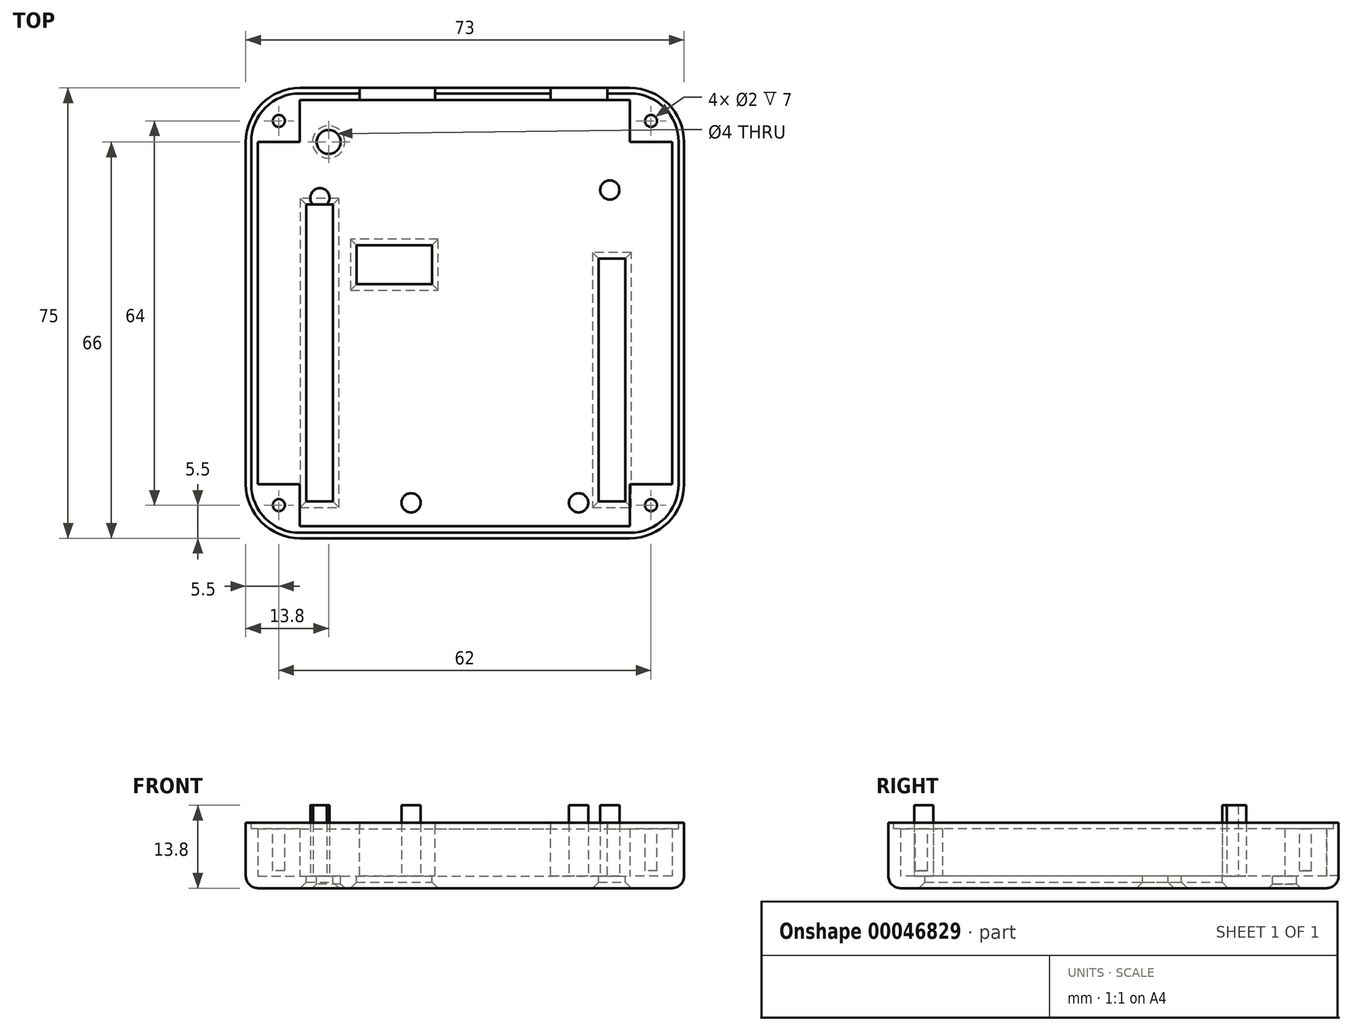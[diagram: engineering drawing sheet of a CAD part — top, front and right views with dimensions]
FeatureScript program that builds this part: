
annotation { "Feature Type Name" : "Feature", "Feature Type Description" : "" }
export const myFeature = defineFeature(function(context is Context, id is Id, definition is map)
    precondition{}
    {
        {
            var Q0;
            Q0=qCreatedBy(makeId("Top.planeOp"),FACE);
            var sketch = newSketch(context, id + "F0", { "sketchPlane" : qUnion([Q0])});
            skLineSegment(sketch, "E0.bottom", {"start": v(-27.5, 38.5) * mm, "end": v(27.5, 38.5) * mm});
            skLineSegment(sketch, "E0.top", {"start": v(-27.5, -36.5) * mm, "end": v(27.5, -36.5) * mm});
            skLineSegment(sketch, "E0.left", {"start": v(-36.5, 29.5) * mm, "end": v(-36.5, -27.5) * mm});
            skLineSegment(sketch, "E0.right", {"start": v(36.5, 29.5) * mm, "end": v(36.5, -27.5) * mm});
            skPoint(sketch, "E1.visualSharp", {"position": v(-36.5, 38.5) * mm});
            skArc(sketch, "E1.filletArc", {"start": v(-27.5, 38.5) * mm, "mid": v(-33.86, 35.86) * mm, "end": v(-36.5, 29.5) * mm});
            skPoint(sketch, "E2.visualSharp", {"position": v(36.5, 38.5) * mm});
            skArc(sketch, "E2.filletArc", {"start": v(36.5, 29.5) * mm, "mid": v(33.86, 35.86) * mm, "end": v(27.5, 38.5) * mm});
            skPoint(sketch, "E3.visualSharp", {"position": v(36.5, -36.5) * mm});
            skArc(sketch, "E3.filletArc", {"start": v(27.5, -36.5) * mm, "mid": v(33.86, -33.86) * mm, "end": v(36.5, -27.5) * mm});
            skPoint(sketch, "E4.visualSharp", {"position": v(-36.5, -36.5) * mm});
            skArc(sketch, "E4.filletArc", {"start": v(-36.5, -27.5) * mm, "mid": v(-33.86, -33.86) * mm, "end": v(-27.5, -36.5) * mm});
            skSolve(sketch);
        }
        {
            var Q0;
            Q0 = qSketchRegion(id + "F0", true);
            extrude(context, id + "F1", {"entities" : qUnion([Q0]), "depth" : 2 * mm});
        }
        {
            var Q0;
            Q0=makeQuery(id+"F1.opExtrude","CAP_FACE",FACE,{"disambiguationData":[OSD([sQuery(id+"F0.wireOp",EDGE,"E0.bottom"),sQuery(id+"F0.wireOp",EDGE,"E0.top"),sQuery(id+"F0.wireOp",EDGE,"E0.left"),sQuery(id+"F0.wireOp",EDGE,"E0.right"),sQuery(id+"F0.wireOp",EDGE,"E1.filletArc"),sQuery(id+"F0.wireOp",EDGE,"E2.filletArc"),sQuery(id+"F0.wireOp",EDGE,"E3.filletArc"),sQuery(id+"F0.wireOp",EDGE,"E4.filletArc")])],"isStart":false});
            var sketch = newSketch(context, id + "F2", { "sketchPlane" : qUnion([Q0])});
            skCircle(sketch, "E5.MirrorC", {"center": v(-24.16, 20.2) * mm, "radius": 1.6 * mm});
            skCircle(sketch, "E6.MirrorC", {"center": v(24.14, 21.5) * mm, "radius": 1.6 * mm});
            skCircle(sketch, "E7.MirrorC", {"center": v(18.94, -30.6) * mm, "radius": 1.6 * mm});
            skCircle(sketch, "E8.MirrorC", {"center": v(-8.96, -30.6) * mm, "radius": 1.6 * mm});
            skSolve(sketch);
        }
        {
            var Q0;
            Q0 = qSketchRegion(id + "F2", true);
            extrude(context, id + "F3", {"entities" : qUnion([Q0]), "operationType" : NewBodyOperationType.ADD, "depth" : 11.8 * mm});
        }
        {
            var Q0;
            Q0=makeQuery(id+"F1.opExtrude","CAP_FACE",FACE,{"disambiguationData":[OSD([sQuery(id+"F0.wireOp",EDGE,"E0.bottom"),sQuery(id+"F0.wireOp",EDGE,"E0.top"),sQuery(id+"F0.wireOp",EDGE,"E0.left"),sQuery(id+"F0.wireOp",EDGE,"E0.right"),sQuery(id+"F0.wireOp",EDGE,"E1.filletArc"),sQuery(id+"F0.wireOp",EDGE,"E2.filletArc"),sQuery(id+"F0.wireOp",EDGE,"E3.filletArc"),sQuery(id+"F0.wireOp",EDGE,"E4.filletArc")])],"isStart":false});
            var sketch = newSketch(context, id + "F4", { "sketchPlane" : qUnion([Q0])});
            skLineSegment(sketch, "E9", {"start": v(-27.5, 36.5) * mm, "end": v(27.5, 36.5) * mm});
            skLineSegment(sketch, "E10", {"start": v(-34.5, 29.5) * mm, "end": v(-34.5, -27.5) * mm});
            skLineSegment(sketch, "E11", {"start": v(-27.5, -34.5) * mm, "end": v(27.5, -34.5) * mm});
            skLineSegment(sketch, "E12", {"start": v(34.5, -27.5) * mm, "end": v(34.5, 29.5) * mm});
            skArc(sketch, "E13", {"start": v(-27.5, 36.5) * mm, "mid": v(-32.45, 34.45) * mm, "end": v(-34.5, 29.5) * mm});
            skArc(sketch, "E14", {"start": v(27.5, -34.5) * mm, "mid": v(32.45, -32.45) * mm, "end": v(34.5, -27.5) * mm});
            skArc(sketch, "E15", {"start": v(-34.5, -27.5) * mm, "mid": v(-32.45, -32.45) * mm, "end": v(-27.5, -34.5) * mm});
            skArc(sketch, "E16", {"start": v(34.5, 29.5) * mm, "mid": v(32.45, 34.45) * mm, "end": v(27.5, 36.5) * mm});
            skLineSegment(sketch, "E17.0", {"start": v(-27.5, 38.5) * mm, "end": v(27.5, 38.5) * mm});
            skArc(sketch, "E17.1", {"start": v(36.5, 29.5) * mm, "mid": v(33.86, 35.86) * mm, "end": v(27.5, 38.5) * mm});
            skLineSegment(sketch, "E17.2", {"start": v(36.5, 29.5) * mm, "end": v(36.5, -27.5) * mm});
            skArc(sketch, "E17.3", {"start": v(27.5, -36.5) * mm, "mid": v(33.86, -33.86) * mm, "end": v(36.5, -27.5) * mm});
            skLineSegment(sketch, "E17.4", {"start": v(-27.5, -36.5) * mm, "end": v(27.5, -36.5) * mm});
            skArc(sketch, "E17.5", {"start": v(-36.5, -27.5) * mm, "mid": v(-33.86, -33.86) * mm, "end": v(-27.5, -36.5) * mm});
            skLineSegment(sketch, "E17.6", {"start": v(-36.5, 29.5) * mm, "end": v(-36.5, -27.5) * mm});
            skArc(sketch, "E17.7", {"start": v(-27.5, 38.5) * mm, "mid": v(-33.86, 35.86) * mm, "end": v(-36.5, 29.5) * mm});
            skSolve(sketch);
        }
        {
            var Q0;
            Q0 = qSketchRegion(id + "F4", true);
            extrude(context, id + "F5", {"entities" : qUnion([Q0]), "operationType" : NewBodyOperationType.ADD, "depth" : 8.9 * mm});
        }
        {
            var Q0;
            Q0=makeQuery(id+"F5.opExtrude","CAP_FACE",FACE,{"disambiguationData":[OSD([sQuery(id+"F4.wireOp",EDGE,"E9"),sQuery(id+"F4.wireOp",EDGE,"E10"),sQuery(id+"F4.wireOp",EDGE,"E11"),sQuery(id+"F4.wireOp",EDGE,"E12"),sQuery(id+"F4.wireOp",EDGE,"E13"),sQuery(id+"F4.wireOp",EDGE,"E14"),sQuery(id+"F4.wireOp",EDGE,"E15"),sQuery(id+"F4.wireOp",EDGE,"E16"),sQuery(id+"F4.wireOp",EDGE,"E17.0"),sQuery(id+"F4.wireOp",EDGE,"E17.1"),sQuery(id+"F4.wireOp",EDGE,"E17.2"),sQuery(id+"F4.wireOp",EDGE,"E17.3"),sQuery(id+"F4.wireOp",EDGE,"E17.4"),sQuery(id+"F4.wireOp",EDGE,"E17.5"),sQuery(id+"F4.wireOp",EDGE,"E17.6"),sQuery(id+"F4.wireOp",EDGE,"E17.7")])],"isStart":false});
            var sketch = newSketch(context, id + "F6", { "sketchPlane" : qUnion([Q0])});
            skLineSegment(sketch, "E18", {"start": v(-27.5, 37.6) * mm, "end": v(27.5, 37.6) * mm});
            skLineSegment(sketch, "E19", {"start": v(-27.5, -35.6) * mm, "end": v(27.5, -35.6) * mm});
            skLineSegment(sketch, "E20", {"start": v(-35.6, 29.5) * mm, "end": v(-35.6, -27.5) * mm});
            skLineSegment(sketch, "E21", {"start": v(35.6, 29.5) * mm, "end": v(35.6, -27.5) * mm});
            skLineSegment(sketch, "E22.0", {"start": v(-27.5, 36.5) * mm, "end": v(27.5, 36.5) * mm});
            skArc(sketch, "E22.1", {"start": v(34.5, 29.5) * mm, "mid": v(32.45, 34.45) * mm, "end": v(27.5, 36.5) * mm});
            skLineSegment(sketch, "E22.2", {"start": v(34.5, -27.5) * mm, "end": v(34.5, 29.5) * mm});
            skArc(sketch, "E22.3", {"start": v(27.5, -34.5) * mm, "mid": v(32.45, -32.45) * mm, "end": v(34.5, -27.5) * mm});
            skLineSegment(sketch, "E22.4", {"start": v(-27.5, -34.5) * mm, "end": v(27.5, -34.5) * mm});
            skArc(sketch, "E22.5", {"start": v(-34.5, -27.5) * mm, "mid": v(-32.45, -32.45) * mm, "end": v(-27.5, -34.5) * mm});
            skLineSegment(sketch, "E22.6", {"start": v(-34.5, 29.5) * mm, "end": v(-34.5, -27.5) * mm});
            skArc(sketch, "E22.7", {"start": v(-27.5, 36.5) * mm, "mid": v(-32.45, 34.45) * mm, "end": v(-34.5, 29.5) * mm});
            skArc(sketch, "E23", {"start": v(-27.5, 37.6) * mm, "mid": v(-33.23, 35.23) * mm, "end": v(-35.6, 29.5) * mm});
            skArc(sketch, "E24", {"start": v(35.6, 29.5) * mm, "mid": v(33.23, 35.23) * mm, "end": v(27.5, 37.6) * mm});
            skArc(sketch, "E25", {"start": v(27.5, -35.6) * mm, "mid": v(33.23, -33.23) * mm, "end": v(35.6, -27.5) * mm});
            skArc(sketch, "E26", {"start": v(-35.6, -27.5) * mm, "mid": v(-33.23, -33.23) * mm, "end": v(-27.5, -35.6) * mm});
            skSolve(sketch);
        }
        {
            var Q0;
            Q0 = qSketchRegion(id + "F6", true);
            extrude(context, id + "F7", {"entities" : qUnion([Q0]), "operationType" : NewBodyOperationType.REMOVE, "oppositeDirection" : true, "depth" : 1 * mm});
        }
        {
            var Q0;
            Q0=makeQuery(id+"F5.opExtrude","CAP_FACE",FACE,{"disambiguationData":[OSD([sQuery(id+"F4.wireOp",EDGE,"E9"),sQuery(id+"F4.wireOp",EDGE,"E10"),sQuery(id+"F4.wireOp",EDGE,"E11"),sQuery(id+"F4.wireOp",EDGE,"E12"),sQuery(id+"F4.wireOp",EDGE,"E13"),sQuery(id+"F4.wireOp",EDGE,"E14"),sQuery(id+"F4.wireOp",EDGE,"E15"),sQuery(id+"F4.wireOp",EDGE,"E16"),sQuery(id+"F4.wireOp",EDGE,"E17.0"),sQuery(id+"F4.wireOp",EDGE,"E17.1"),sQuery(id+"F4.wireOp",EDGE,"E17.2"),sQuery(id+"F4.wireOp",EDGE,"E17.3"),sQuery(id+"F4.wireOp",EDGE,"E17.4"),sQuery(id+"F4.wireOp",EDGE,"E17.5"),sQuery(id+"F4.wireOp",EDGE,"E17.6"),sQuery(id+"F4.wireOp",EDGE,"E17.7")])],"isStart":false});
            var sketch = newSketch(context, id + "F8", { "sketchPlane" : qUnion([Q0])});
            skLineSegment(sketch, "E27.bottom", {"start": v(-17.56, 38.5) * mm, "end": v(-4.96, 38.5) * mm});
            skLineSegment(sketch, "E27.top", {"start": v(-17.56, 36.5) * mm, "end": v(-4.96, 36.5) * mm});
            skLineSegment(sketch, "E27.left", {"start": v(-17.56, 38.5) * mm, "end": v(-17.56, 36.5) * mm});
            skLineSegment(sketch, "E27.right", {"start": v(-4.96, 38.5) * mm, "end": v(-4.96, 36.5) * mm});
            skLineSegment(sketch, "E28.bottom", {"start": v(14.24, 38.5) * mm, "end": v(23.74, 38.5) * mm});
            skLineSegment(sketch, "E28.top", {"start": v(14.24, 36.5) * mm, "end": v(23.74, 36.5) * mm});
            skLineSegment(sketch, "E28.left", {"start": v(14.24, 38.5) * mm, "end": v(14.24, 36.5) * mm});
            skLineSegment(sketch, "E28.right", {"start": v(23.74, 38.5) * mm, "end": v(23.74, 36.5) * mm});
            skSolve(sketch);
        }
        {
            var Q0;
            Q0 = qSketchRegion(id + "F8", true);
            extrude(context, id + "F9", {"entities" : qUnion([Q0]), "operationType" : NewBodyOperationType.REMOVE, "oppositeDirection" : true, "depth" : 8.8 * mm});
        }
        {
            var Q0;
            Q0=makeQuery(id+"F1.opExtrude","CAP_FACE",FACE,{"disambiguationData":[OSD([sQuery(id+"F0.wireOp",EDGE,"E0.bottom"),sQuery(id+"F0.wireOp",EDGE,"E0.top"),sQuery(id+"F0.wireOp",EDGE,"E0.left"),sQuery(id+"F0.wireOp",EDGE,"E0.right"),sQuery(id+"F0.wireOp",EDGE,"E1.filletArc"),sQuery(id+"F0.wireOp",EDGE,"E2.filletArc"),sQuery(id+"F0.wireOp",EDGE,"E3.filletArc"),sQuery(id+"F0.wireOp",EDGE,"E4.filletArc")])],"isStart":false});
            var sketch = newSketch(context, id + "F10", { "sketchPlane" : qUnion([Q0])});
            skLineSegment(sketch, "E29.bottom", {"start": v(-26.46, 19.1) * mm, "end": v(-21.96, 19.1) * mm});
            skLineSegment(sketch, "E29.top", {"start": v(-26.46, -30.4) * mm, "end": v(-21.96, -30.4) * mm});
            skLineSegment(sketch, "E29.left", {"start": v(-26.46, 19.1) * mm, "end": v(-26.46, -30.4) * mm});
            skLineSegment(sketch, "E29.right", {"start": v(-21.96, 19.1) * mm, "end": v(-21.96, -30.4) * mm});
            skLineSegment(sketch, "E30.bottom", {"start": v(22.24, 10.1) * mm, "end": v(26.74, 10.1) * mm});
            skLineSegment(sketch, "E30.top", {"start": v(22.24, -30.4) * mm, "end": v(26.74, -30.4) * mm});
            skLineSegment(sketch, "E30.left", {"start": v(22.24, 10.1) * mm, "end": v(22.24, -30.4) * mm});
            skLineSegment(sketch, "E30.right", {"start": v(26.74, 10.1) * mm, "end": v(26.74, -30.4) * mm});
            skSolve(sketch);
        }
        {
            var Q0;
            Q0 = qSketchRegion(id + "F10", true);
            extrude(context, id + "F11", {"entities" : qUnion([Q0]), "operationType" : NewBodyOperationType.REMOVE, "oppositeDirection" : true, "depth" : 10 * mm});
        }
        {
            var Q0;
            Q0 = qSketchRegion(id + "F10", true);
            extrude(context, id + "F12", {"entities" : qUnion([Q0]), "operationType" : NewBodyOperationType.REMOVE, "depth" : 15 * mm});
        }
        {
            var Q0;
            Q0=makeQuery(id+"F1.opExtrude","CAP_FACE",FACE,{"disambiguationData":[OSD([sQuery(id+"F0.wireOp",EDGE,"E0.bottom"),sQuery(id+"F0.wireOp",EDGE,"E0.top"),sQuery(id+"F0.wireOp",EDGE,"E0.left"),sQuery(id+"F0.wireOp",EDGE,"E0.right"),sQuery(id+"F0.wireOp",EDGE,"E1.filletArc"),sQuery(id+"F0.wireOp",EDGE,"E2.filletArc"),sQuery(id+"F0.wireOp",EDGE,"E3.filletArc"),sQuery(id+"F0.wireOp",EDGE,"E4.filletArc")])],"isStart":false});
            var sketch = newSketch(context, id + "F13", { "sketchPlane" : qUnion([Q0])});
            skLineSegment(sketch, "E31", {"start": v(-27.5, 36.5) * mm, "end": v(-27.5, 29.5) * mm});
            skLineSegment(sketch, "E32", {"start": v(-27.5, 29.5) * mm, "end": v(-34.5, 29.5) * mm});
            skArc(sketch, "E33.0", {"start": v(-27.5, 36.5) * mm, "mid": v(-32.45, 34.45) * mm, "end": v(-34.5, 29.5) * mm});
            skArc(sketch, "E33.1", {"start": v(34.5, 29.5) * mm, "mid": v(32.45, 34.45) * mm, "end": v(27.5, 36.5) * mm});
            skArc(sketch, "E33.2", {"start": v(27.5, -34.5) * mm, "mid": v(32.45, -32.45) * mm, "end": v(34.5, -27.5) * mm});
            skArc(sketch, "E33.3", {"start": v(-34.5, -27.5) * mm, "mid": v(-32.45, -32.45) * mm, "end": v(-27.5, -34.5) * mm});
            skLineSegment(sketch, "E34", {"start": v(-34.5, -27.5) * mm, "end": v(-27.5, -27.5) * mm});
            skLineSegment(sketch, "E35", {"start": v(-27.5, -27.5) * mm, "end": v(-27.5, -34.5) * mm});
            skLineSegment(sketch, "E36", {"start": v(34.5, -27.5) * mm, "end": v(27.5, -27.5) * mm});
            skLineSegment(sketch, "E37", {"start": v(27.5, -34.5) * mm, "end": v(27.5, -27.5) * mm});
            skLineSegment(sketch, "E38", {"start": v(27.5, 36.5) * mm, "end": v(27.5, 29.5) * mm});
            skLineSegment(sketch, "E39", {"start": v(34.5, 29.5) * mm, "end": v(27.5, 29.5) * mm});
            skSolve(sketch);
        }
        {
            var Q0;
            Q0 = qSketchRegion(id + "F13", true);
            extrude(context, id + "F14", {"entities" : qUnion([Q0]), "operationType" : NewBodyOperationType.ADD, "depth" : 7.9 * mm});
        }
        {
            var Q0;
            {var subQ0=sQuery(id+"F6.wireOp",EDGE,"E18");var subQ1=sQuery(id+"F6.wireOp",EDGE,"E19");var subQ2=sQuery(id+"F6.wireOp",EDGE,"E20");var subQ3=sQuery(id+"F6.wireOp",EDGE,"E21");var subQ4=sQuery(id+"F6.wireOp",EDGE,"E23");var subQ5=sQuery(id+"F6.wireOp",EDGE,"E24");var subQ6=sQuery(id+"F6.wireOp",EDGE,"E25");var subQ7=sQuery(id+"F6.wireOp",EDGE,"E26");Q0=makeQuery(id+"F14.boolean.opBoolean","MERGE",FACE,{"derivedFrom":[makeQuery(id+"F9.boolean.opBoolean","SPLIT",FACE,{"disambiguationData":[TD([makeQuery(id+"F5.opExtrude","SWEPT_FACE",FACE,{"disambiguationData":[OSD([sQuery(id+"F4.wireOp",EDGE,"E10")])]})])],"derivedFrom":makeQuery(id+"F7.boolean.opBoolean","COPY",FACE,{"derivedFrom":makeQuery(id+"F7.opExtrude","CAP_FACE",FACE,{"disambiguationData":[OSD([subQ0,subQ1,subQ2,subQ3,sQuery(id+"F6.wireOp",EDGE,"E22.0"),sQuery(id+"F6.wireOp",EDGE,"E22.1"),sQuery(id+"F6.wireOp",EDGE,"E22.2"),sQuery(id+"F6.wireOp",EDGE,"E22.3"),sQuery(id+"F6.wireOp",EDGE,"E22.4"),sQuery(id+"F6.wireOp",EDGE,"E22.5"),sQuery(id+"F6.wireOp",EDGE,"E22.6"),sQuery(id+"F6.wireOp",EDGE,"E22.7"),subQ4,subQ5,subQ6,subQ7])],"isStart":false})})}),makeQuery(id+"F14.opExtrude","CAP_FACE",FACE,{"disambiguationData":[OSD([sQuery(id+"F13.wireOp",EDGE,"E31"),sQuery(id+"F13.wireOp",EDGE,"E32"),sQuery(id+"F13.wireOp",EDGE,"E33.0")])],"isStart":false}),makeQuery(id+"F14.opExtrude","CAP_FACE",FACE,{"disambiguationData":[OSD([sQuery(id+"F13.wireOp",EDGE,"E33.1"),sQuery(id+"F13.wireOp",EDGE,"E38"),sQuery(id+"F13.wireOp",EDGE,"E39")])],"isStart":false}),makeQuery(id+"F14.opExtrude","CAP_FACE",FACE,{"disambiguationData":[OSD([sQuery(id+"F13.wireOp",EDGE,"E33.2"),sQuery(id+"F13.wireOp",EDGE,"E36"),sQuery(id+"F13.wireOp",EDGE,"E37")])],"isStart":false}),makeQuery(id+"F14.opExtrude","CAP_FACE",FACE,{"disambiguationData":[OSD([sQuery(id+"F13.wireOp",EDGE,"E33.3"),sQuery(id+"F13.wireOp",EDGE,"E34"),sQuery(id+"F13.wireOp",EDGE,"E35")])],"isStart":false})]});}
            var sketch = newSketch(context, id + "F15", { "sketchPlane" : qUnion([Q0])});
            skCircle(sketch, "E40", {"center": v(-31, 33) * mm, "radius": 1 * mm});
            skCircle(sketch, "E41", {"center": v(31, 33) * mm, "radius": 1 * mm});
            skCircle(sketch, "E42", {"center": v(31, -31) * mm, "radius": 1 * mm});
            skCircle(sketch, "E43", {"center": v(-31, -31) * mm, "radius": 1 * mm});
            skSolve(sketch);
        }
        {
            var Q0;
            Q0 = qSketchRegion(id + "F15", true);
            extrude(context, id + "F16", {"entities" : qUnion([Q0]), "operationType" : NewBodyOperationType.REMOVE, "oppositeDirection" : true, "depth" : 7 * mm});
        }
        {
            var Q0;
            Q0=makeQuery(id+"F1.opExtrude","CAP_FACE",FACE,{"disambiguationData":[OSD([sQuery(id+"F0.wireOp",EDGE,"E0.bottom"),sQuery(id+"F0.wireOp",EDGE,"E0.top"),sQuery(id+"F0.wireOp",EDGE,"E0.left"),sQuery(id+"F0.wireOp",EDGE,"E0.right"),sQuery(id+"F0.wireOp",EDGE,"E1.filletArc"),sQuery(id+"F0.wireOp",EDGE,"E2.filletArc"),sQuery(id+"F0.wireOp",EDGE,"E3.filletArc"),sQuery(id+"F0.wireOp",EDGE,"E4.filletArc")])],"isStart":false});
            var sketch = newSketch(context, id + "F17", { "sketchPlane" : qUnion([Q0])});
            skLineSegment(sketch, "E44.bottom", {"start": v(-18.06, 12.33) * mm, "end": v(-5.46, 12.33) * mm});
            skLineSegment(sketch, "E44.top", {"start": v(-18.06, 5.83) * mm, "end": v(-5.46, 5.83) * mm});
            skLineSegment(sketch, "E44.left", {"start": v(-18.06, 12.33) * mm, "end": v(-18.06, 5.83) * mm});
            skLineSegment(sketch, "E44.right", {"start": v(-5.46, 12.33) * mm, "end": v(-5.46, 5.83) * mm});
            skSolve(sketch);
        }
        {
            var Q0;
            Q0 = qSketchRegion(id + "F17", true);
            extrude(context, id + "F18", {"entities" : qUnion([Q0]), "operationType" : NewBodyOperationType.REMOVE, "oppositeDirection" : true, "depth" : 4 * mm});
        }
        {
            var Q0;
            Q0=makeQuery(id+"F11.boolean.opBoolean","INTERSECT",EDGE,{"derivedFrom":[makeQuery(id+"F1.opExtrude","CAP_FACE",FACE,{"disambiguationData":[OSD([sQuery(id+"F0.wireOp",EDGE,"E0.bottom"),sQuery(id+"F0.wireOp",EDGE,"E0.top"),sQuery(id+"F0.wireOp",EDGE,"E0.left"),sQuery(id+"F0.wireOp",EDGE,"E0.right"),sQuery(id+"F0.wireOp",EDGE,"E1.filletArc"),sQuery(id+"F0.wireOp",EDGE,"E2.filletArc"),sQuery(id+"F0.wireOp",EDGE,"E3.filletArc"),sQuery(id+"F0.wireOp",EDGE,"E4.filletArc")])],"isStart":true}),makeQuery(id+"F11.opExtrude","SWEPT_FACE",FACE,{"disambiguationData":[OSD([sQuery(id+"F10.wireOp",EDGE,"E29.left")])]})]});
            var Q1;
            Q1=makeQuery(id+"F11.boolean.opBoolean","INTERSECT",EDGE,{"derivedFrom":[makeQuery(id+"F1.opExtrude","CAP_FACE",FACE,{"disambiguationData":[OSD([sQuery(id+"F0.wireOp",EDGE,"E0.bottom"),sQuery(id+"F0.wireOp",EDGE,"E0.top"),sQuery(id+"F0.wireOp",EDGE,"E0.left"),sQuery(id+"F0.wireOp",EDGE,"E0.right"),sQuery(id+"F0.wireOp",EDGE,"E1.filletArc"),sQuery(id+"F0.wireOp",EDGE,"E2.filletArc"),sQuery(id+"F0.wireOp",EDGE,"E3.filletArc"),sQuery(id+"F0.wireOp",EDGE,"E4.filletArc")])],"isStart":true}),makeQuery(id+"F11.opExtrude","SWEPT_FACE",FACE,{"disambiguationData":[OSD([sQuery(id+"F10.wireOp",EDGE,"E29.bottom")])]})]});
            var Q2;
            Q2=makeQuery(id+"F11.boolean.opBoolean","INTERSECT",EDGE,{"derivedFrom":[makeQuery(id+"F1.opExtrude","CAP_FACE",FACE,{"disambiguationData":[OSD([sQuery(id+"F0.wireOp",EDGE,"E0.bottom"),sQuery(id+"F0.wireOp",EDGE,"E0.top"),sQuery(id+"F0.wireOp",EDGE,"E0.left"),sQuery(id+"F0.wireOp",EDGE,"E0.right"),sQuery(id+"F0.wireOp",EDGE,"E1.filletArc"),sQuery(id+"F0.wireOp",EDGE,"E2.filletArc"),sQuery(id+"F0.wireOp",EDGE,"E3.filletArc"),sQuery(id+"F0.wireOp",EDGE,"E4.filletArc")])],"isStart":true}),makeQuery(id+"F11.opExtrude","SWEPT_FACE",FACE,{"disambiguationData":[OSD([sQuery(id+"F10.wireOp",EDGE,"E29.right")])]})]});
            var Q3;
            Q3=makeQuery(id+"F11.boolean.opBoolean","INTERSECT",EDGE,{"derivedFrom":[makeQuery(id+"F1.opExtrude","CAP_FACE",FACE,{"disambiguationData":[OSD([sQuery(id+"F0.wireOp",EDGE,"E0.bottom"),sQuery(id+"F0.wireOp",EDGE,"E0.top"),sQuery(id+"F0.wireOp",EDGE,"E0.left"),sQuery(id+"F0.wireOp",EDGE,"E0.right"),sQuery(id+"F0.wireOp",EDGE,"E1.filletArc"),sQuery(id+"F0.wireOp",EDGE,"E2.filletArc"),sQuery(id+"F0.wireOp",EDGE,"E3.filletArc"),sQuery(id+"F0.wireOp",EDGE,"E4.filletArc")])],"isStart":true}),makeQuery(id+"F11.opExtrude","SWEPT_FACE",FACE,{"disambiguationData":[OSD([sQuery(id+"F10.wireOp",EDGE,"E29.top")])]})]});
            var Q4;
            Q4=makeQuery(id+"F18.boolean.opBoolean","INTERSECT",EDGE,{"derivedFrom":[makeQuery(id+"F1.opExtrude","CAP_FACE",FACE,{"disambiguationData":[OSD([sQuery(id+"F0.wireOp",EDGE,"E0.bottom"),sQuery(id+"F0.wireOp",EDGE,"E0.top"),sQuery(id+"F0.wireOp",EDGE,"E0.left"),sQuery(id+"F0.wireOp",EDGE,"E0.right"),sQuery(id+"F0.wireOp",EDGE,"E1.filletArc"),sQuery(id+"F0.wireOp",EDGE,"E2.filletArc"),sQuery(id+"F0.wireOp",EDGE,"E3.filletArc"),sQuery(id+"F0.wireOp",EDGE,"E4.filletArc")])],"isStart":true}),makeQuery(id+"F18.opExtrude","SWEPT_FACE",FACE,{"disambiguationData":[OSD([sQuery(id+"F17.wireOp",EDGE,"E44.top")])]})]});
            var Q5;
            Q5=makeQuery(id+"F18.boolean.opBoolean","INTERSECT",EDGE,{"derivedFrom":[makeQuery(id+"F1.opExtrude","CAP_FACE",FACE,{"disambiguationData":[OSD([sQuery(id+"F0.wireOp",EDGE,"E0.bottom"),sQuery(id+"F0.wireOp",EDGE,"E0.top"),sQuery(id+"F0.wireOp",EDGE,"E0.left"),sQuery(id+"F0.wireOp",EDGE,"E0.right"),sQuery(id+"F0.wireOp",EDGE,"E1.filletArc"),sQuery(id+"F0.wireOp",EDGE,"E2.filletArc"),sQuery(id+"F0.wireOp",EDGE,"E3.filletArc"),sQuery(id+"F0.wireOp",EDGE,"E4.filletArc")])],"isStart":true}),makeQuery(id+"F18.opExtrude","SWEPT_FACE",FACE,{"disambiguationData":[OSD([sQuery(id+"F17.wireOp",EDGE,"E44.left")])]})]});
            var Q6;
            Q6=makeQuery(id+"F18.boolean.opBoolean","INTERSECT",EDGE,{"derivedFrom":[makeQuery(id+"F1.opExtrude","CAP_FACE",FACE,{"disambiguationData":[OSD([sQuery(id+"F0.wireOp",EDGE,"E0.bottom"),sQuery(id+"F0.wireOp",EDGE,"E0.top"),sQuery(id+"F0.wireOp",EDGE,"E0.left"),sQuery(id+"F0.wireOp",EDGE,"E0.right"),sQuery(id+"F0.wireOp",EDGE,"E1.filletArc"),sQuery(id+"F0.wireOp",EDGE,"E2.filletArc"),sQuery(id+"F0.wireOp",EDGE,"E3.filletArc"),sQuery(id+"F0.wireOp",EDGE,"E4.filletArc")])],"isStart":true}),makeQuery(id+"F18.opExtrude","SWEPT_FACE",FACE,{"disambiguationData":[OSD([sQuery(id+"F17.wireOp",EDGE,"E44.bottom")])]})]});
            var Q7;
            Q7=makeQuery(id+"F18.boolean.opBoolean","INTERSECT",EDGE,{"derivedFrom":[makeQuery(id+"F1.opExtrude","CAP_FACE",FACE,{"disambiguationData":[OSD([sQuery(id+"F0.wireOp",EDGE,"E0.bottom"),sQuery(id+"F0.wireOp",EDGE,"E0.top"),sQuery(id+"F0.wireOp",EDGE,"E0.left"),sQuery(id+"F0.wireOp",EDGE,"E0.right"),sQuery(id+"F0.wireOp",EDGE,"E1.filletArc"),sQuery(id+"F0.wireOp",EDGE,"E2.filletArc"),sQuery(id+"F0.wireOp",EDGE,"E3.filletArc"),sQuery(id+"F0.wireOp",EDGE,"E4.filletArc")])],"isStart":true}),makeQuery(id+"F18.opExtrude","SWEPT_FACE",FACE,{"disambiguationData":[OSD([sQuery(id+"F17.wireOp",EDGE,"E44.right")])]})]});
            var Q8;
            Q8=makeQuery(id+"F11.boolean.opBoolean","INTERSECT",EDGE,{"derivedFrom":[makeQuery(id+"F1.opExtrude","CAP_FACE",FACE,{"disambiguationData":[OSD([sQuery(id+"F0.wireOp",EDGE,"E0.bottom"),sQuery(id+"F0.wireOp",EDGE,"E0.top"),sQuery(id+"F0.wireOp",EDGE,"E0.left"),sQuery(id+"F0.wireOp",EDGE,"E0.right"),sQuery(id+"F0.wireOp",EDGE,"E1.filletArc"),sQuery(id+"F0.wireOp",EDGE,"E2.filletArc"),sQuery(id+"F0.wireOp",EDGE,"E3.filletArc"),sQuery(id+"F0.wireOp",EDGE,"E4.filletArc")])],"isStart":true}),makeQuery(id+"F11.opExtrude","SWEPT_FACE",FACE,{"disambiguationData":[OSD([sQuery(id+"F10.wireOp",EDGE,"E30.left")])]})]});
            var Q9;
            Q9=makeQuery(id+"F11.boolean.opBoolean","INTERSECT",EDGE,{"derivedFrom":[makeQuery(id+"F1.opExtrude","CAP_FACE",FACE,{"disambiguationData":[OSD([sQuery(id+"F0.wireOp",EDGE,"E0.bottom"),sQuery(id+"F0.wireOp",EDGE,"E0.top"),sQuery(id+"F0.wireOp",EDGE,"E0.left"),sQuery(id+"F0.wireOp",EDGE,"E0.right"),sQuery(id+"F0.wireOp",EDGE,"E1.filletArc"),sQuery(id+"F0.wireOp",EDGE,"E2.filletArc"),sQuery(id+"F0.wireOp",EDGE,"E3.filletArc"),sQuery(id+"F0.wireOp",EDGE,"E4.filletArc")])],"isStart":true}),makeQuery(id+"F11.opExtrude","SWEPT_FACE",FACE,{"disambiguationData":[OSD([sQuery(id+"F10.wireOp",EDGE,"E30.right")])]})]});
            var Q10;
            Q10=makeQuery(id+"F11.boolean.opBoolean","INTERSECT",EDGE,{"derivedFrom":[makeQuery(id+"F1.opExtrude","CAP_FACE",FACE,{"disambiguationData":[OSD([sQuery(id+"F0.wireOp",EDGE,"E0.bottom"),sQuery(id+"F0.wireOp",EDGE,"E0.top"),sQuery(id+"F0.wireOp",EDGE,"E0.left"),sQuery(id+"F0.wireOp",EDGE,"E0.right"),sQuery(id+"F0.wireOp",EDGE,"E1.filletArc"),sQuery(id+"F0.wireOp",EDGE,"E2.filletArc"),sQuery(id+"F0.wireOp",EDGE,"E3.filletArc"),sQuery(id+"F0.wireOp",EDGE,"E4.filletArc")])],"isStart":true}),makeQuery(id+"F11.opExtrude","SWEPT_FACE",FACE,{"disambiguationData":[OSD([sQuery(id+"F10.wireOp",EDGE,"E30.bottom")])]})]});
            var Q11;
            Q11=makeQuery(id+"F11.boolean.opBoolean","INTERSECT",EDGE,{"derivedFrom":[makeQuery(id+"F1.opExtrude","CAP_FACE",FACE,{"disambiguationData":[OSD([sQuery(id+"F0.wireOp",EDGE,"E0.bottom"),sQuery(id+"F0.wireOp",EDGE,"E0.top"),sQuery(id+"F0.wireOp",EDGE,"E0.left"),sQuery(id+"F0.wireOp",EDGE,"E0.right"),sQuery(id+"F0.wireOp",EDGE,"E1.filletArc"),sQuery(id+"F0.wireOp",EDGE,"E2.filletArc"),sQuery(id+"F0.wireOp",EDGE,"E3.filletArc"),sQuery(id+"F0.wireOp",EDGE,"E4.filletArc")])],"isStart":true}),makeQuery(id+"F11.opExtrude","SWEPT_FACE",FACE,{"disambiguationData":[OSD([sQuery(id+"F10.wireOp",EDGE,"E30.top")])]})]});
            chamfer(context, id + "F19", {"entities" : qUnion([Q0, Q1, Q2, Q3, Q4, Q5, Q6, Q7, Q8, Q9, Q10, Q11]), "width" : 1 * mm, "tangentPropagation" : true});
        }
        {
            var Q0;
            Q0=makeQuery(id+"F1.opExtrude","CAP_FACE",FACE,{"disambiguationData":[OSD([sQuery(id+"F0.wireOp",EDGE,"E0.bottom"),sQuery(id+"F0.wireOp",EDGE,"E0.top"),sQuery(id+"F0.wireOp",EDGE,"E0.left"),sQuery(id+"F0.wireOp",EDGE,"E0.right"),sQuery(id+"F0.wireOp",EDGE,"E1.filletArc"),sQuery(id+"F0.wireOp",EDGE,"E2.filletArc"),sQuery(id+"F0.wireOp",EDGE,"E3.filletArc"),sQuery(id+"F0.wireOp",EDGE,"E4.filletArc")])],"isStart":false});
            var sketch = newSketch(context, id + "F20", { "sketchPlane" : qUnion([Q0])});
            skCircle(sketch, "E45", {"center": v(-22.7, 29.5) * mm, "radius": 2 * mm});
            skSolve(sketch);
        }
        {
            var Q0;
            Q0 = qSketchRegion(id + "F20", true);
            extrude(context, id + "F21", {"entities" : qUnion([Q0]), "operationType" : NewBodyOperationType.REMOVE, "oppositeDirection" : true, "depth" : 4 * mm});
        }
        {
            var Q0;
            Q0=makeQuery(id+"F1.opExtrude","CAP_EDGE",EDGE,{"disambiguationData":[OSD([sQuery(id+"F0.wireOp",EDGE,"E0.bottom")])],"isStart":true});
            fillet(context, id + "F22", {"entities" : qUnion([Q0]), "radius" : 2 * mm, "tangentPropagation" : true, "allowEdgeOverflow" : false});
        }
        {
            var Q0;
            Q0=makeQuery(id+"F21.boolean.opBoolean","INTERSECT",EDGE,{"derivedFrom":[makeQuery(id+"F1.opExtrude","CAP_FACE",FACE,{"disambiguationData":[OSD([sQuery(id+"F0.wireOp",EDGE,"E0.bottom"),sQuery(id+"F0.wireOp",EDGE,"E0.top"),sQuery(id+"F0.wireOp",EDGE,"E0.left"),sQuery(id+"F0.wireOp",EDGE,"E0.right"),sQuery(id+"F0.wireOp",EDGE,"E1.filletArc"),sQuery(id+"F0.wireOp",EDGE,"E2.filletArc"),sQuery(id+"F0.wireOp",EDGE,"E3.filletArc"),sQuery(id+"F0.wireOp",EDGE,"E4.filletArc")])],"isStart":true}),makeQuery(id+"F21.opExtrude","SWEPT_FACE",FACE,{"disambiguationData":[OSD([sQuery(id+"F20.wireOp",EDGE,"E45")])]})]});
            chamfer(context, id + "F23", {"entities" : qUnion([Q0]), "width" : .7 * mm, "tangentPropagation" : true});
        }
    });
